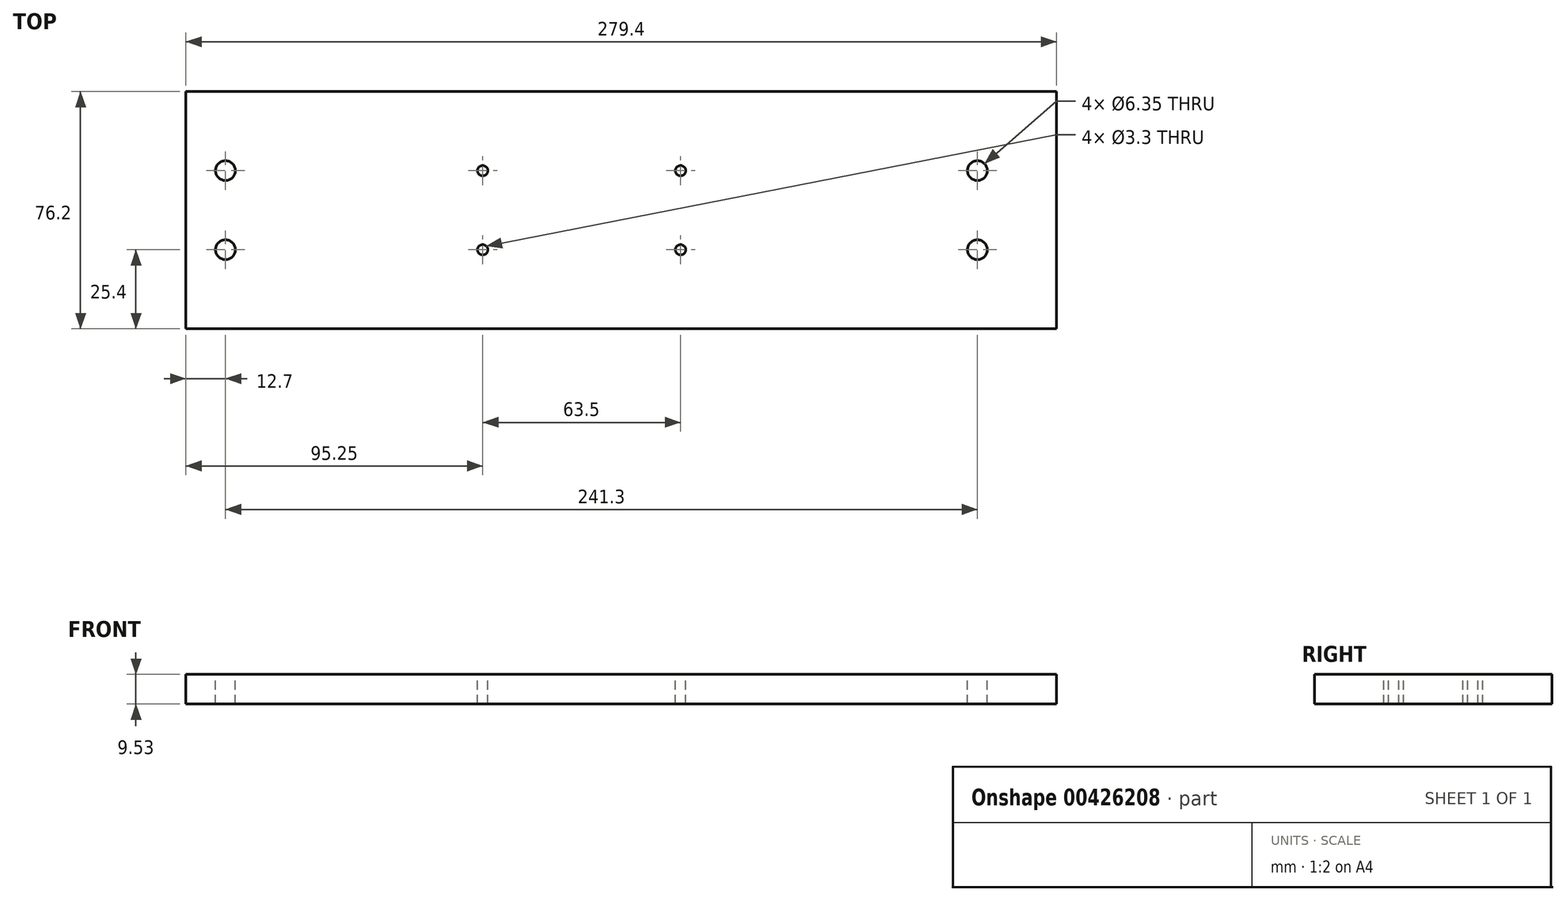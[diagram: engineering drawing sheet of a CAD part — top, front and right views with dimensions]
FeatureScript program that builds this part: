
annotation { "Feature Type Name" : "Feature", "Feature Type Description" : "" }
export const myFeature = defineFeature(function(context is Context, id is Id, definition is map)
    precondition{}
    {
        {
            var Q0;
            Q0=qCreatedBy(makeId("Top.planeOp"),FACE);
            var sketch = newSketch(context, id + "F0", { "sketchPlane" : qUnion([Q0])});
            skLineSegment(sketch, "E0.bottom", {"start": v(0, 0) * mm, "end": v(279.4, 0) * mm});
            skLineSegment(sketch, "E0.top", {"start": v(0, 76.2) * mm, "end": v(279.4, 76.2) * mm});
            skLineSegment(sketch, "E0.left", {"start": v(0, 0) * mm, "end": v(0, 76.2) * mm});
            skLineSegment(sketch, "E0.right", {"start": v(279.4, 0) * mm, "end": v(279.4, 76.2) * mm});
            skSolve(sketch);
        }
        {
            var Q0;
            Q0 = qSketchRegion(id + "F0", true);
            extrude(context, id + "F1", {"entities" : qUnion([Q0]), "depth" : 9.52 * mm});
        }
        {
            var Q0;
            Q0=makeQuery(id+"F1.opExtrude","CAP_FACE",FACE,{"disambiguationData":[OSD([sQuery(id+"F0.wireOp",EDGE,"E0.bottom"),sQuery(id+"F0.wireOp",EDGE,"E0.top"),sQuery(id+"F0.wireOp",EDGE,"E0.left"),sQuery(id+"F0.wireOp",EDGE,"E0.right")])],"isStart":false});
            var sketch = newSketch(context, id + "F2", { "sketchPlane" : qUnion([Q0])});
            skCircle(sketch, "E1", {"center": v(12.7, 50.8) * mm, "radius": 3.18 * mm});
            skCircle(sketch, "E2", {"center": v(12.7, 25.4) * mm, "radius": 3.18 * mm});
            skCircle(sketch, "E3", {"center": v(254, 50.8) * mm, "radius": 3.18 * mm});
            skCircle(sketch, "E4", {"center": v(254, 25.4) * mm, "radius": 3.18 * mm});
            skSolve(sketch);
        }
        {
            var Q0;
            Q0 = qSketchRegion(id + "F2", true);
            extrude(context, id + "F3", {"entities" : qUnion([Q0]), "operationType" : NewBodyOperationType.REMOVE, "oppositeDirection" : true, "depth" : 25.4 * mm});
        }
        {
            var Q0;
            Q0=makeQuery(id+"F1.opExtrude","CAP_FACE",FACE,{"disambiguationData":[OSD([sQuery(id+"F0.wireOp",EDGE,"E0.bottom"),sQuery(id+"F0.wireOp",EDGE,"E0.top"),sQuery(id+"F0.wireOp",EDGE,"E0.left"),sQuery(id+"F0.wireOp",EDGE,"E0.right")])],"isStart":false});
            var sketch = newSketch(context, id + "F4", { "sketchPlane" : qUnion([Q0])});
            skCircle(sketch, "E5", {"center": v(95.25, 50.8) * mm, "radius": 1.65 * mm});
            skCircle(sketch, "E6", {"center": v(95.25, 25.4) * mm, "radius": 1.65 * mm});
            skCircle(sketch, "E7", {"center": v(158.75, 50.8) * mm, "radius": 1.65 * mm});
            skCircle(sketch, "E8", {"center": v(158.75, 25.4) * mm, "radius": 1.65 * mm});
            skSolve(sketch);
        }
        {
            var Q0;
            Q0 = qSketchRegion(id + "F4", true);
            extrude(context, id + "F5", {"entities" : qUnion([Q0]), "operationType" : NewBodyOperationType.REMOVE, "oppositeDirection" : true, "depth" : 25.4 * mm});
        }
    });
